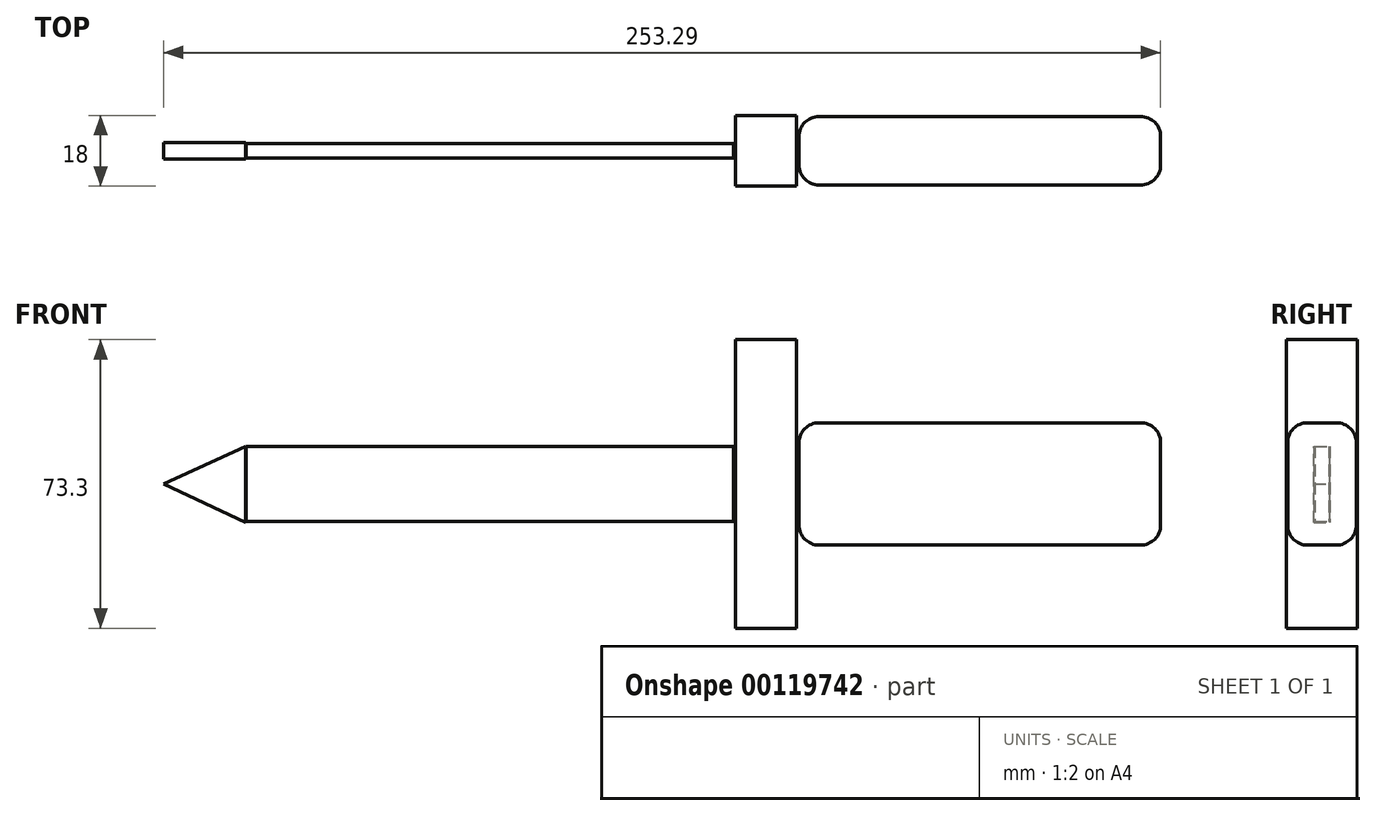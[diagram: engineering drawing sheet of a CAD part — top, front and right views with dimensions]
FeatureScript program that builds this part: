
annotation { "Feature Type Name" : "Feature", "Feature Type Description" : "" }
export const myFeature = defineFeature(function(context is Context, id is Id, definition is map)
    precondition{}
    {
        {
            var Q0;
            Q0=qCreatedBy(makeId("Front.planeOp"),FACE);
            var sketch = newSketch(context, id + "F0", { "sketchPlane" : qUnion([Q0])});
            skLineSegment(sketch, "E0.bottom", {"start": v(61.9, 9.56) * mm, "end": v(-61.9, 9.56) * mm});
            skLineSegment(sketch, "E0.top", {"start": v(61.9, -9.56) * mm, "end": v(-61.9, -9.56) * mm});
            skLineSegment(sketch, "E0.left", {"start": v(61.9, 9.56) * mm, "end": v(61.9, -9.56) * mm});
            skLineSegment(sketch, "E0.right", {"start": v(-61.9, 9.56) * mm, "end": v(-61.9, -9.56) * mm});
            skPoint(sketch, "E0.middle", {"position": v(0, 0) * mm});
            skSolve(sketch);
        }
        {
            var Q0;
            Q0=qCreatedBy(makeId("Front.planeOp"),FACE);
            var sketch = newSketch(context, id + "F1", { "sketchPlane" : qUnion([Q0])});
            skLineSegment(sketch, "E1.bottom", {"start": v(77.87, 36.65) * mm, "end": v(62.47, 36.65) * mm});
            skLineSegment(sketch, "E1.top", {"start": v(77.87, -36.65) * mm, "end": v(62.47, -36.65) * mm});
            skLineSegment(sketch, "E1.left", {"start": v(77.87, 36.65) * mm, "end": v(77.87, -36.65) * mm});
            skLineSegment(sketch, "E1.right", {"start": v(62.47, 36.65) * mm, "end": v(62.47, -36.65) * mm});
            skPoint(sketch, "E1.middle", {"position": v(70.17, 0) * mm});
            skSolve(sketch);
        }
        {
            var Q0;
            Q0=qCreatedBy(makeId("Front.planeOp"),FACE);
            var sketch = newSketch(context, id + "F2", { "sketchPlane" : qUnion([Q0])});
            skLineSegment(sketch, "E2", {"start": v(-82.88, 0) * mm, "end": v(-62.06, 9.56) * mm});
            skLineSegment(sketch, "E3", {"start": v(-62.06, 9.56) * mm, "end": v(-62.06, -9.84) * mm});
            skLineSegment(sketch, "E4", {"start": v(-62.06, -9.84) * mm, "end": v(-82.88, 0) * mm});
            skSolve(sketch);
        }
        {
            var Q0;
            Q0=qCreatedBy(makeId("Front.planeOp"),FACE);
            var sketch = newSketch(context, id + "F3", { "sketchPlane" : qUnion([Q0])});
            skLineSegment(sketch, "E5.bottom", {"start": v(170.41, 15.55) * mm, "end": v(78.56, 15.55) * mm});
            skLineSegment(sketch, "E5.top", {"start": v(170.41, -15.55) * mm, "end": v(78.56, -15.55) * mm});
            skLineSegment(sketch, "E5.left", {"start": v(170.41, 15.55) * mm, "end": v(170.41, -15.55) * mm});
            skLineSegment(sketch, "E5.right", {"start": v(78.56, 15.55) * mm, "end": v(78.56, -15.55) * mm});
            skPoint(sketch, "E5.middle", {"position": v(124.49, 0) * mm});
            skSolve(sketch);
        }
        {
            var Q0;
            Q0=makeQuery(id+"F2.imprint","IMPRINT",FACE,{"disambiguationData":[TD([[makeQuery(id+"F2.imprint","IMPRINT",EDGE,{"derivedFrom":sQuery(id+"F2.wireOp",EDGE,"E2")}),-1.0]])]});
            extrude(context, id + "F4", {"entities" : qUnion([Q0]), "endBound" : BoundingType.SYMMETRIC, "depth" : 4.12 * mm});
        }
        {
            var Q0;
            Q0=makeQuery(id+"F1.imprint","IMPRINT",FACE,{"disambiguationData":[TD([[makeQuery(id+"F1.imprint","IMPRINT",EDGE,{"derivedFrom":sQuery(id+"F1.wireOp",EDGE,"E1.bottom")}),1.0]])]});
            extrude(context, id + "F5", {"entities" : qUnion([Q0]), "endBound" : BoundingType.SYMMETRIC, "depth" : 18 * mm});
        }
        {
            var Q0;
            Q0=makeQuery(id+"F0.imprint","IMPRINT",FACE,{"disambiguationData":[TD([[makeQuery(id+"F0.imprint","IMPRINT",EDGE,{"derivedFrom":sQuery(id+"F0.wireOp",EDGE,"E0.bottom")}),1.0]])]});
            extrude(context, id + "F6", {"entities" : qUnion([Q0]), "endBound" : BoundingType.SYMMETRIC, "depth" : 3.6 * mm});
        }
        {
            var Q0;
            Q0=makeQuery(id+"F3.imprint","IMPRINT",FACE,{"disambiguationData":[TD([[makeQuery(id+"F3.imprint","IMPRINT",EDGE,{"derivedFrom":sQuery(id+"F3.wireOp",EDGE,"E5.bottom")}),1.0]])]});
            extrude(context, id + "F7", {"entities" : qUnion([Q0]), "endBound" : BoundingType.SYMMETRIC, "depth" : 17.43 * mm});
        }
        {
            var Q0;
            Q0=makeQuery(id+"F7.opExtrude","CAP_FACE",FACE,{"disambiguationData":[OSD([sQuery(id+"F3.wireOp",EDGE,"E5.bottom"),sQuery(id+"F3.wireOp",EDGE,"E5.top"),sQuery(id+"F3.wireOp",EDGE,"E5.left"),sQuery(id+"F3.wireOp",EDGE,"E5.right")])],"isStart":false});
            var Q1;
            Q1=makeQuery(id+"F7.opExtrude","CAP_FACE",FACE,{"disambiguationData":[OSD([sQuery(id+"F3.wireOp",EDGE,"E5.bottom"),sQuery(id+"F3.wireOp",EDGE,"E5.top"),sQuery(id+"F3.wireOp",EDGE,"E5.left"),sQuery(id+"F3.wireOp",EDGE,"E5.right")])],"isStart":true});
            var Q2;
            Q2=makeQuery(id+"F7.opExtrude","SWEPT_FACE",FACE,{"disambiguationData":[OSD([sQuery(id+"F3.wireOp",EDGE,"E5.bottom")])]});
            var Q3;
            Q3=makeQuery(id+"F7.opExtrude","SWEPT_FACE",FACE,{"disambiguationData":[OSD([sQuery(id+"F3.wireOp",EDGE,"E5.top")])]});
            fillet(context, id + "F8", {"entities" : qUnion([Q0, Q1, Q2, Q3]), "radius" : 5.08 * mm, "tangentPropagation" : true, "allowEdgeOverflow" : false});
        }
    });
